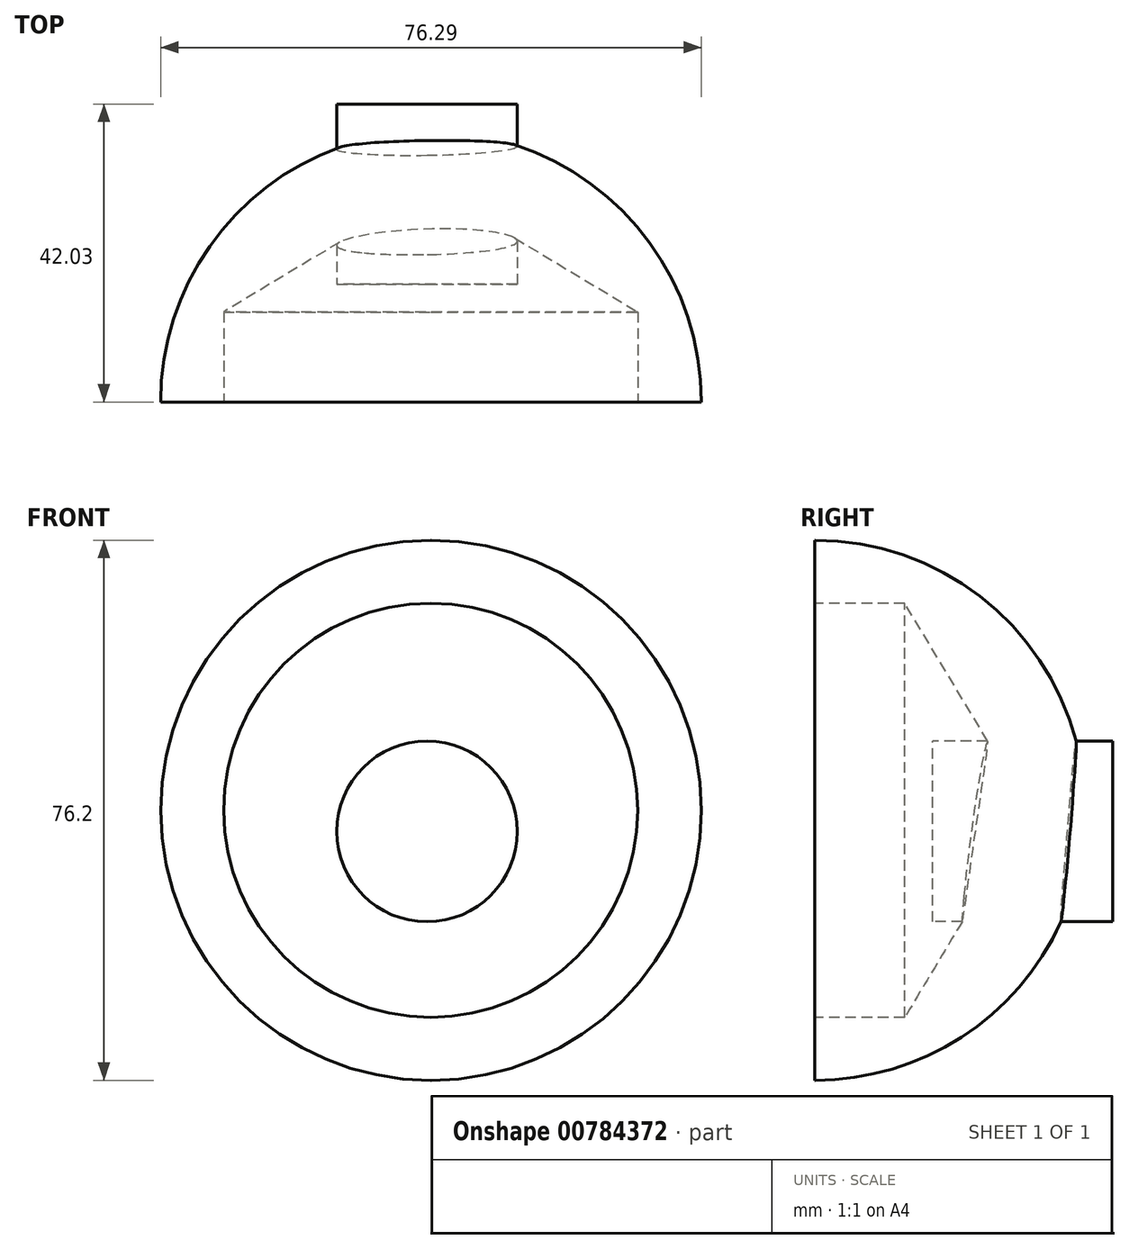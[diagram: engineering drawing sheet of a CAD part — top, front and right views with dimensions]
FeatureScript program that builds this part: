
annotation { "Feature Type Name" : "Feature", "Feature Type Description" : "" }
export const myFeature = defineFeature(function(context is Context, id is Id, definition is map)
    precondition{}
    {
        {
            var Q0;
            Q0=qCreatedBy(makeId("Top.planeOp"),FACE);
            var sketch = newSketch(context, id + "F0", { "sketchPlane" : qUnion([Q0])});
            skLineSegment(sketch, "E0.bottom", {"start": v(-39.2, 21.51) * mm, "end": v(37.1, 21.51) * mm});
            skLineSegment(sketch, "E0.top", {"start": v(-39.2, -16.63) * mm, "end": v(37.1, -16.63) * mm});
            skLineSegment(sketch, "E0.left", {"start": v(-39.2, 21.51) * mm, "end": v(-39.2, -16.63) * mm});
            skLineSegment(sketch, "E0.right", {"start": v(37.1, 21.51) * mm, "end": v(37.1, -16.63) * mm});
            skSolve(sketch);
        }
        {
            var Q0;
            Q0=makeQuery(id+"F0.imprint","IMPRINT",FACE,{"disambiguationData":[TD([[makeQuery(id+"F0.imprint","IMPRINT",EDGE,{"derivedFrom":sQuery(id+"F0.wireOp",EDGE,"E0.bottom")}),-1.0]])]});
            extrude(context, id + "F1", {"entities" : qUnion([Q0]), "depth" : 76.2 * mm, "offsetDistance" : 25.4 * mm});
        }
        {
            var Q0;
            Q0=makeQuery(id+"F1.opExtrude","CAP_EDGE",EDGE,{"disambiguationData":[OSD([sQuery(id+"F0.wireOp",EDGE,"E0.left")])],"isStart":false});
            var Q1;
            Q1=makeQuery(id+"F1.opExtrude","CAP_EDGE",EDGE,{"disambiguationData":[OSD([sQuery(id+"F0.wireOp",EDGE,"E0.left")])],"isStart":true});
            var Q2;
            Q2=makeQuery(id+"F1.opExtrude","CAP_EDGE",EDGE,{"disambiguationData":[OSD([sQuery(id+"F0.wireOp",EDGE,"E0.right")])],"isStart":false});
            var Q3;
            Q3=makeQuery(id+"F1.opExtrude","CAP_EDGE",EDGE,{"disambiguationData":[OSD([sQuery(id+"F0.wireOp",EDGE,"E0.right")])],"isStart":true});
            fillet(context, id + "F2", {"entities" : qUnion([Q0, Q1, Q2, Q3]), "radius" : 38.1 * mm, "tangentPropagation" : true, "allowEdgeOverflow" : false});
        }
        {
            var Q0;
            Q0=makeQuery(id+"F1.opExtrude","SWEPT_FACE",FACE,{"disambiguationData":[OSD([sQuery(id+"F0.wireOp",EDGE,"E0.top")])]});
            var sketch = newSketch(context, id + "F3", { "sketchPlane" : qUnion([Q0])});
            skCircle(sketch, "E1", {"center": v(-1.1, 38.1) * mm, "radius": 29.24 * mm});
            skSolve(sketch);
        }
        {
            var Q0;
            Q0=sQuery(id+"F3.wireOp",VERTEX,"E1.center");
            var Q1;
            Q1=makeQuery(id+"F1.opExtrude","SWEPT_BODY",BODY,{"disambiguationData":[OSD([sQuery(id+"F0.wireOp",EDGE,"E0.bottom"),sQuery(id+"F0.wireOp",EDGE,"E0.top"),sQuery(id+"F0.wireOp",EDGE,"E0.left"),sQuery(id+"F0.wireOp",EDGE,"E0.right")])]});
            hole(context, id + "F4", {"style" : HoleStyle.SIMPLE, "endStyle" : HoleEndStyle.BLIND, "holeDiameter" : 58.42 * mm, "majorDiameter" : 6.35 * mm, "holeDepth" : 12.7 * mm, "isTappedThrough" : true, "tappedDepth" : 12.7 * mm, "tapClearance" : 3, "locations" : qUnion([Q0]), "scope" : qUnion([Q1])});
        }
        {
            var Q0;
            Q0=makeQuery(id+"F2.opFillet","BLEND_EDGE",EDGE,{"blendedFrom":[makeQuery(id+"F1.opExtrude","CAP_EDGE",EDGE,{"disambiguationData":[OSD([sQuery(id+"F0.wireOp",EDGE,"E0.left")])],"isStart":true}),makeQuery(id+"F1.opExtrude","SWEPT_FACE",FACE,{"disambiguationData":[OSD([sQuery(id+"F0.wireOp",EDGE,"E0.bottom")])]})],"blendedInto":[makeQuery(id+"F1.opExtrude","SWEPT_FACE",FACE,{"disambiguationData":[OSD([sQuery(id+"F0.wireOp",EDGE,"E0.bottom")])]})]});
            var Q1;
            Q1=makeQuery(id+"F2.opFillet","BLEND_EDGE",EDGE,{"blendedFrom":[makeQuery(id+"F1.opExtrude","CAP_EDGE",EDGE,{"disambiguationData":[OSD([sQuery(id+"F0.wireOp",EDGE,"E0.right")])],"isStart":true}),makeQuery(id+"F1.opExtrude","SWEPT_FACE",FACE,{"disambiguationData":[OSD([sQuery(id+"F0.wireOp",EDGE,"E0.bottom")])]})],"blendedInto":[makeQuery(id+"F1.opExtrude","SWEPT_FACE",FACE,{"disambiguationData":[OSD([sQuery(id+"F0.wireOp",EDGE,"E0.bottom")])]})]});
            fillet(context, id + "F5", {"entities" : qUnion([Q0, Q1]), "radius" : 38.1 * mm, "tangentPropagation" : true, "allowEdgeOverflow" : false});
        }
        {
            var Q0;
            Q0=qCreatedBy(makeId("Front.planeOp"),FACE);
            var sketch = newSketch(context, id + "F6", { "sketchPlane" : qUnion([Q0])});
            skCircle(sketch, "E2", {"center": v(-1.6, 35.1) * mm, "radius": 12.74 * mm});
            skSolve(sketch);
        }
        {
            var Q0;
            Q0 = qSketchRegion(id + "F6", true);
            extrude(context, id + "F7", {"entities" : qUnion([Q0]), "operationType" : NewBodyOperationType.ADD, "depth" : -25.4 * mm, "offsetDistance" : 25.4 * mm});
        }
    });
